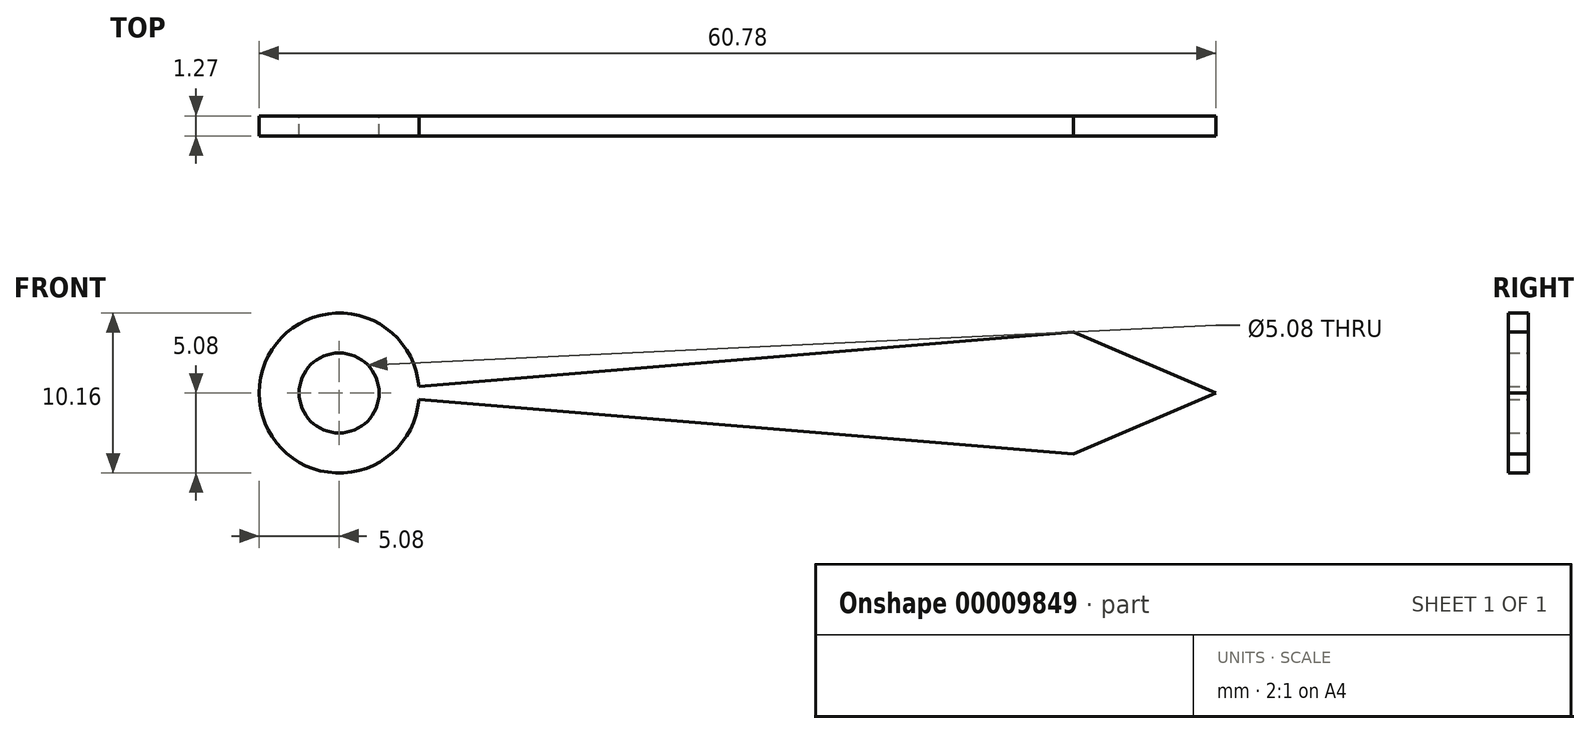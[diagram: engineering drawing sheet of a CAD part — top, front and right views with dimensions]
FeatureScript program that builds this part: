
annotation { "Feature Type Name" : "Feature", "Feature Type Description" : "" }
export const myFeature = defineFeature(function(context is Context, id is Id, definition is map)
    precondition{}
    {
        {
            var Q0;
            Q0=qCreatedBy(makeId("Front.planeOp"),FACE);
            var sketch = newSketch(context, id + "F0", { "sketchPlane" : qUnion([Q0])});
            skCircle(sketch, "E0", {"center": v(0, 0) * mm, "radius": 5.08 * mm});
            skLineSegment(sketch, "E1", {"start": v(0, 0) * mm, "end": v(46.64, 3.88) * mm});
            skLineSegment(sketch, "E2", {"start": v(46.64, 3.88) * mm, "end": v(55.7, 0) * mm});
            skLineSegment(sketch, "E3.0.MirrorCS", {"start": v(46.64, -3.88) * mm, "end": v(55.7, 0) * mm});
            skLineSegment(sketch, "E4.0.MirrorCS", {"start": v(0, 0) * mm, "end": v(46.64, -3.88) * mm});
            skCircle(sketch, "E5", {"center": v(0, 0) * mm, "radius": 2.54 * mm});
            skSolve(sketch);
        }
        {
            var Q0;
            {var subQ1=sQuery(id+"F0.wireOp",EDGE,"E0");var subQ3=sQuery(id+"F0.wireOp",EDGE,"E1");var subQ5=makeQuery(id+"F0.imprint","INTERSECT",VERTEX,{"derivedFrom":[subQ1,subQ3]});Q0=makeQuery(id+"F0.imprint","IMPRINT",FACE,{"disambiguationData":[TD([[makeQuery(id+"F0.imprint","IMPRINT",EDGE,{"disambiguationData":[TD([[subQ5,-1.0]])],"derivedFrom":subQ1}),1.0]])]});}
            var Q1;
            {var subQ4=sQuery(id+"F0.wireOp",EDGE,"E2");Q1=makeQuery(id+"F0.imprint","IMPRINT",FACE,{"disambiguationData":[TD([[makeQuery(id+"F0.imprint","IMPRINT",EDGE,{"derivedFrom":subQ4}),-1.0]])]});}
            var Q2;
            {var subQ3=sQuery(id+"F0.wireOp",EDGE,"E1");var subQ5=sQuery(id+"F0.wireOp",EDGE,"E0");var subQ7=makeQuery(id+"F0.imprint","INTERSECT",VERTEX,{"derivedFrom":[subQ5,subQ3]});Q2=makeQuery(id+"F0.imprint","IMPRINT",FACE,{"disambiguationData":[TD([[makeQuery(id+"F0.imprint","IMPRINT",EDGE,{"disambiguationData":[TD([[subQ7,1.0]])],"derivedFrom":subQ5}),1.0]])]});}
            extrude(context, id + "F1", {"entities" : qUnion([Q0, Q1, Q2]), "depth" : 1.27 * mm});
        }
    });
